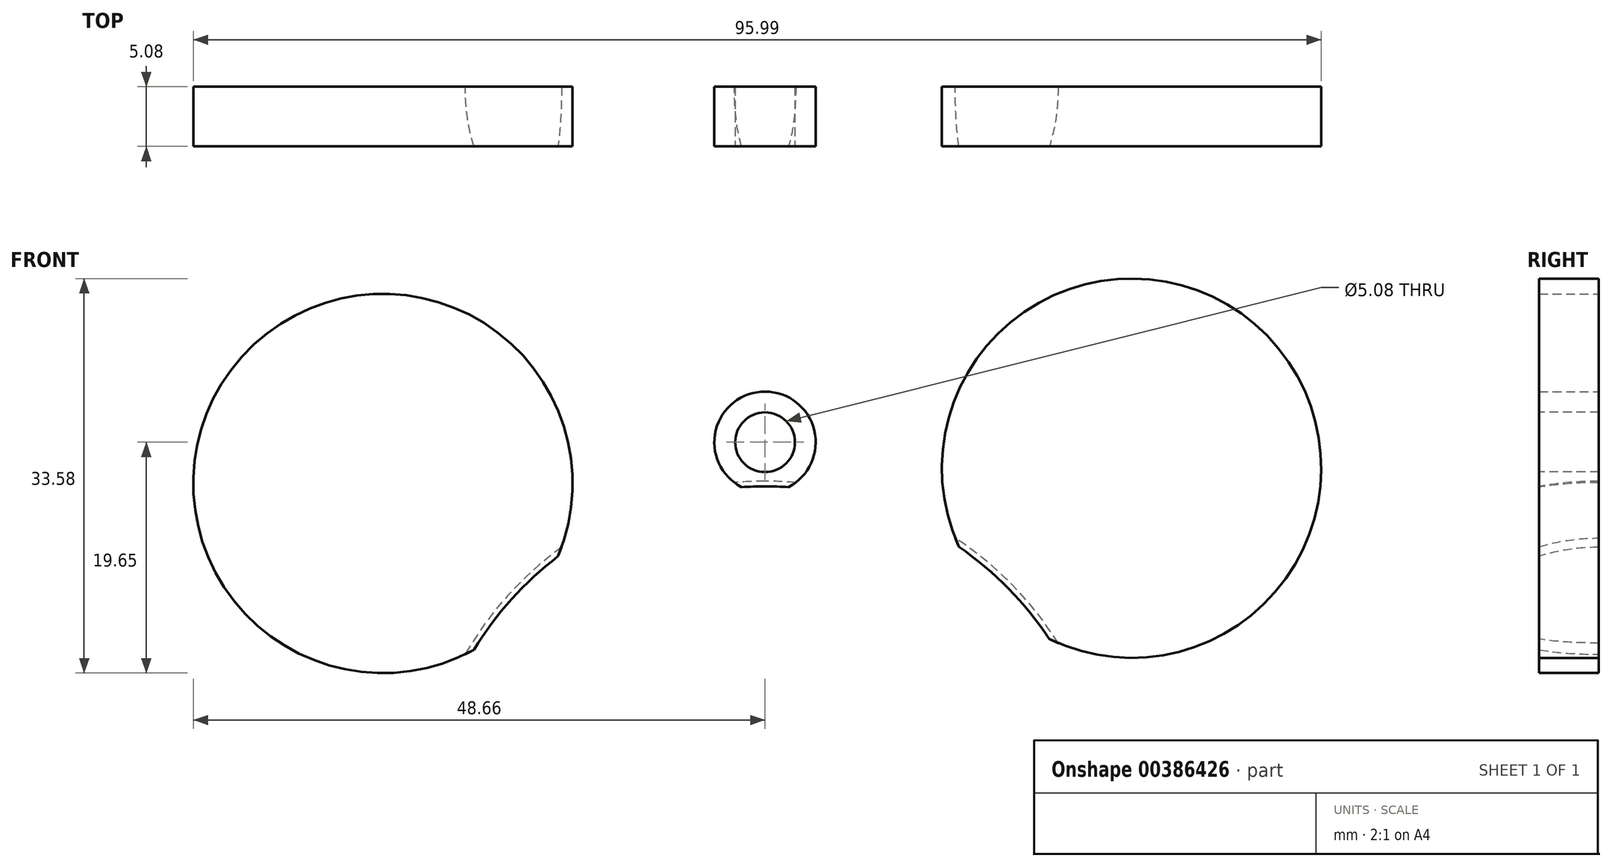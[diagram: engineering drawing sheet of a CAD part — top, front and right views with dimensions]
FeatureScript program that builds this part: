
annotation { "Feature Type Name" : "Feature", "Feature Type Description" : "" }
export const myFeature = defineFeature(function(context is Context, id is Id, definition is map)
    precondition{}
    {
        {
            var Q0;
            Q0=qCreatedBy(makeId("Right.planeOp"),FACE);
            var sketch = newSketch(context, id + "F0", { "sketchPlane" : qUnion([Q0])});
            skArc(sketch, "E0", {"start": v(0, 0) * mm, "mid": v(29.46, 29.46) * mm, "end": v(0, 58.92) * mm});
            skLineSegment(sketch, "E1", {"start": v(0, 58.92) * mm, "end": v(0, 0) * mm});
            skSolve(sketch);
        }
        {
            var Q0;
            Q0=makeQuery(id+"F0.imprint","IMPRINT",FACE,{"disambiguationData":[TD([[makeQuery(id+"F0.imprint","IMPRINT",EDGE,{"derivedFrom":sQuery(id+"F0.wireOp",EDGE,"BfjmkFmi-ORfl-qQVB-7ku5-Pe8sq7gPOb7d")}),1.0]])]});
            var Q1;
            Q1=makeQuery(id+"F0.imprint","IMPRINT",FACE,{"disambiguationData":[TD([[makeQuery(id+"F0.imprint","IMPRINT",EDGE,{"derivedFrom":sQuery(id+"F0.wireOp",EDGE,"E0")}),1.0]])]});
            var Q2;
            Q2=sQuery(id+"F0.wireOp",EDGE,"E1");
            revolve(context, id + "F1", {"entities" : qUnion([Q0, Q1]), "axis" : qUnion([Q2]), "revolveType" : RevolveType.SYMMETRIC, "oppositeDirection" : true, "angle" : 360 * degree});
        }
        {
            var Q0;
            Q0=qCreatedBy(makeId("Front.planeOp"),FACE);
            var sketch = newSketch(context, id + "F2", { "sketchPlane" : qUnion([Q0])});
            skCircle(sketch, "E2", {"center": v(-32.52, 58.72) * mm, "radius": 16.14 * mm});
            skSolve(sketch);
        }
        {
            var Q0;
            Q0=makeQuery(id+"F2.imprint","IMPRINT",FACE,{"disambiguationData":[TD([[makeQuery(id+"F2.imprint","IMPRINT",EDGE,{"derivedFrom":sQuery(id+"F2.wireOp",EDGE,"E2")}),1.0]])]});
            extrude(context, id + "F3", {"entities" : qUnion([Q0]), "operationType" : NewBodyOperationType.ADD, "depth" : 5.08 * mm});
        }
        {
            var Q0;
            Q0=qCreatedBy(makeId("Front.planeOp"),FACE);
            var sketch = newSketch(context, id + "F4", { "sketchPlane" : qUnion([Q0])});
            skCircle(sketch, "E3", {"center": v(31.2, 60.02) * mm, "radius": 16.14 * mm});
            skSolve(sketch);
        }
        {
            var Q0;
            Q0=makeQuery(id+"F4.imprint","IMPRINT",FACE,{"disambiguationData":[TD([[makeQuery(id+"F4.imprint","IMPRINT",EDGE,{"derivedFrom":sQuery(id+"F4.wireOp",EDGE,"E3")}),1.0]])]});
            extrude(context, id + "F5", {"entities" : qUnion([Q0]), "operationType" : NewBodyOperationType.ADD, "depth" : 5.08 * mm});
        }
        {
            var Q0;
            Q0=qCreatedBy(makeId("Front.planeOp"),FACE);
            var sketch = newSketch(context, id + "F6", { "sketchPlane" : qUnion([Q0])});
            skCircle(sketch, "E4", {"center": v(0, 62.23) * mm, "radius": 4.31 * mm});
            skPoint(sketch, "E4.first.point", {"position": v(0, 57.92) * mm});
            skPoint(sketch, "E4.second.point", {"position": v(0, 66.54) * mm});
            skPoint(sketch, "E4.third.point", {"position": v(-2.8, 65.5) * mm});
            skSolve(sketch);
        }
        {
            var Q0;
            Q0 = qSketchRegion(id + "F8", true);
            var Q1;
            Q1 = qSketchRegion(id + "F6", true);
            extrude(context, id + "F7", {"entities" : qUnion([Q0, Q1]), "operationType" : NewBodyOperationType.ADD, "depth" : 5.08 * mm});
        }
        {
            var Q0;
            Q0=makeQuery(id+"F7.opExtrude","CAP_FACE",FACE,{"disambiguationData":[OSD([sQuery(id+"F6.wireOp",EDGE,"E4")])],"isStart":false});
            var sketch = newSketch(context, id + "F8", { "sketchPlane" : qUnion([Q0])});
            skPoint(sketch, "E5", {"position": v(0, 62.23) * mm});
            skSolve(sketch);
        }
        {
            var Q0;
            Q0=sQuery(id+"F8.wireOp",VERTEX,"E5");
            var Q1;
            Q1=makeQuery(id+"F1.opRevolve","SWEPT_BODY",BODY,{"disambiguationData":[OSD([sQuery(id+"F0.wireOp",EDGE,"E0"),sQuery(id+"F0.wireOp",EDGE,"E1")])]});
            hole(context, id + "F9", {"style" : HoleStyle.SIMPLE, "endStyle" : HoleEndStyle.THROUGH, "holeDiameter" : 5.08 * mm, "majorDiameter" : 6.35 * mm, "isTappedThrough" : true, "tappedDepth" : 12.7 * mm, "tapClearance" : 3, "locations" : qUnion([Q0]), "scope" : qUnion([Q1])});
        }
    });
